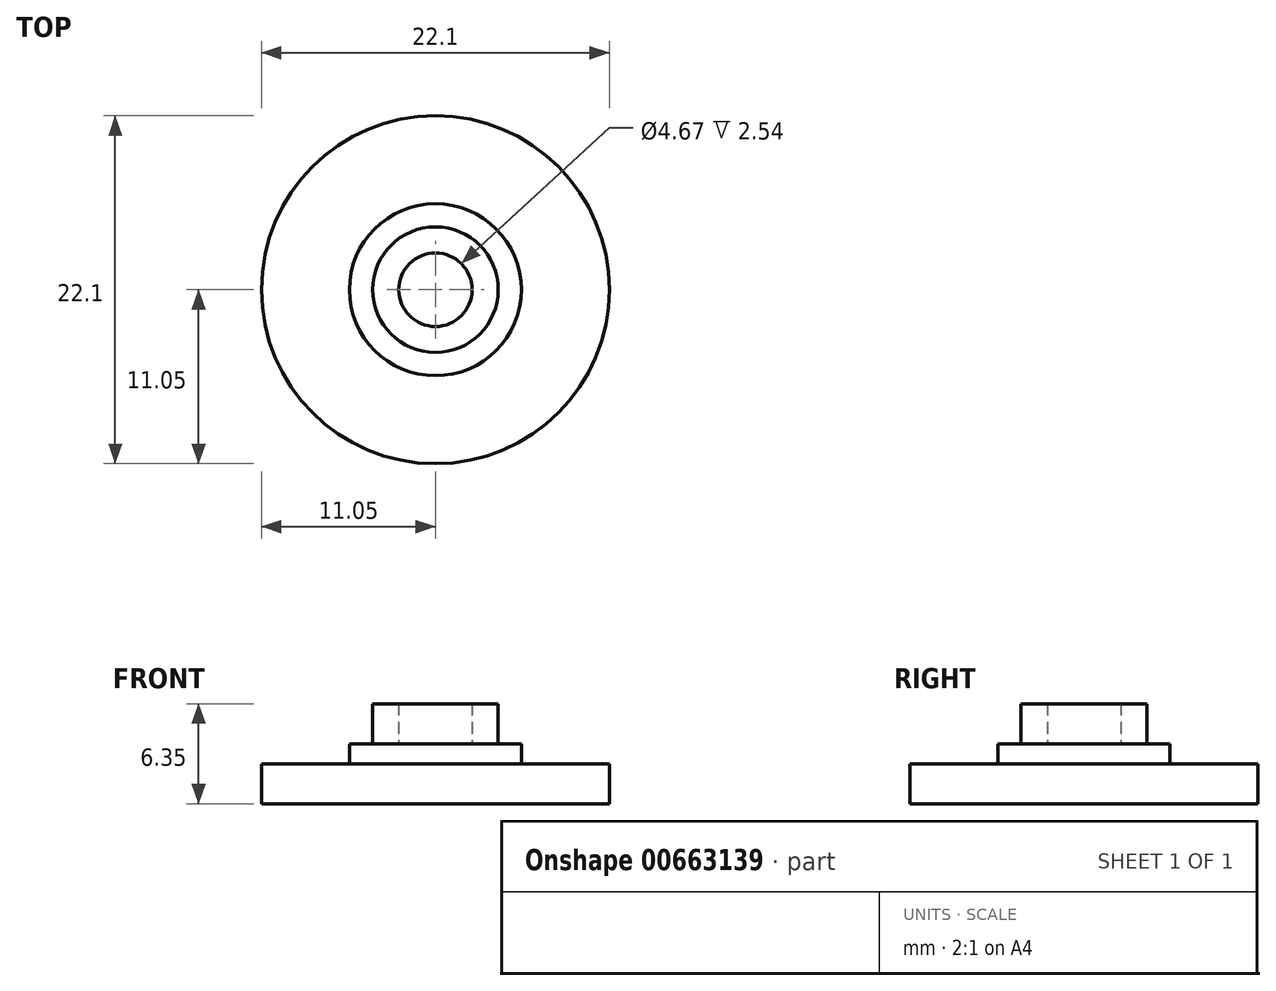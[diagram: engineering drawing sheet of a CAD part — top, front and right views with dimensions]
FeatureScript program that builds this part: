
annotation { "Feature Type Name" : "Feature", "Feature Type Description" : "" }
export const myFeature = defineFeature(function(context is Context, id is Id, definition is map)
    precondition{}
    {
        {
            var Q0;
            Q0=qCreatedBy(makeId("Top.planeOp"),FACE);
            var sketch = newSketch(context, id + "F0", { "sketchPlane" : qUnion([Q0])});
            skCircle(sketch, "E0", {"center": v(0, 0) * mm, "radius": 11.05 * mm});
            skSolve(sketch);
        }
        {
            var Q0;
            Q0 = qSketchRegion(id + "F0", true);
            extrude(context, id + "F1", {"entities" : qUnion([Q0]), "depth" : 2.54 * mm, "offsetDistance" : 25.4 * mm});
        }
        {
            var Q0;
            Q0=qCreatedBy(makeId("Top.planeOp"),FACE);
            var sketch = newSketch(context, id + "F2", { "sketchPlane" : qUnion([Q0])});
            skCircle(sketch, "E1", {"center": v(0, 0) * mm, "radius": 5.46 * mm});
            skSolve(sketch);
        }
        {
            var Q0;
            Q0 = qSketchRegion(id + "F2", true);
            extrude(context, id + "F3", {"entities" : qUnion([Q0]), "operationType" : NewBodyOperationType.ADD, "depth" : 3.8 * mm, "offsetDistance" : 25.4 * mm});
        }
        {
            var Q0;
            Q0=qCreatedBy(makeId("Top.planeOp"),FACE);
            var sketch = newSketch(context, id + "F4", { "sketchPlane" : qUnion([Q0])});
            skCircle(sketch, "E2", {"center": v(0, 0) * mm, "radius": 3.99 * mm});
            skCircle(sketch, "E3", {"center": v(0, 0) * mm, "radius": 2.33 * mm});
            skSolve(sketch);
        }
        {
            var Q0;
            Q0 = qSketchRegion(id + "F4", true);
            extrude(context, id + "F5", {"entities" : qUnion([Q0]), "operationType" : NewBodyOperationType.ADD, "depth" : 6.35 * mm, "offsetDistance" : 25.4 * mm});
        }
    });
